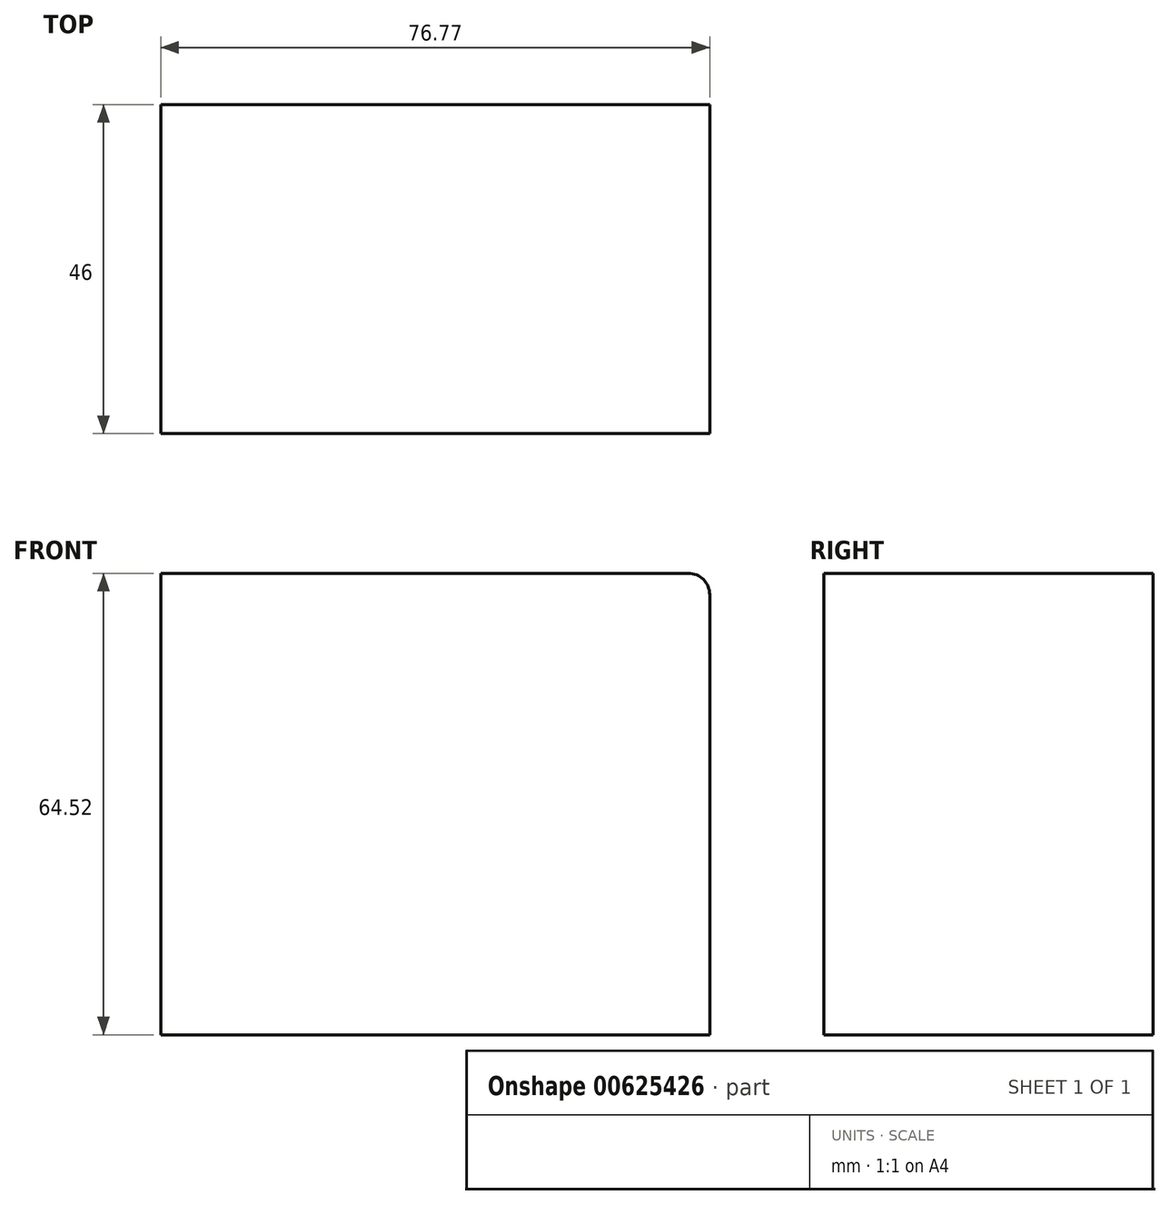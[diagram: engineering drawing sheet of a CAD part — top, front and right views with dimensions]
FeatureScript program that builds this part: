
annotation { "Feature Type Name" : "Feature", "Feature Type Description" : "" }
export const myFeature = defineFeature(function(context is Context, id is Id, definition is map)
    precondition{}
    {
        {
            var Q0;
            Q0=qCreatedBy(makeId("Front.planeOp"),FACE);
            var sketch = newSketch(context, id + "F0", { "sketchPlane" : qUnion([Q0])});
            skLineSegment(sketch, "E0.bottom", {"start": v(-29.7, 32.5) * mm, "end": v(47.07, 32.5) * mm});
            skLineSegment(sketch, "E0.top", {"start": v(-29.7, -32.01) * mm, "end": v(47.07, -32.01) * mm});
            skLineSegment(sketch, "E0.left", {"start": v(-29.7, 32.5) * mm, "end": v(-29.7, -32.01) * mm});
            skLineSegment(sketch, "E0.right", {"start": v(47.07, 32.5) * mm, "end": v(47.07, -32.01) * mm});
            skSolve(sketch);
        }
        {
            var Q0;
            Q0=makeQuery(id+"F0.imprint","IMPRINT",FACE,{"disambiguationData":[TD([[makeQuery(id+"F0.imprint","IMPRINT",EDGE,{"derivedFrom":sQuery(id+"F0.wireOp",EDGE,"E0.bottom")}),-1.0]])]});
            var Q1;
            Q1 = qSketchRegion(id + "F0", true);
            extrude(context, id + "F1", {"entities" : qUnion([Q0, Q1]), "depth" : 46 * mm, "offsetDistance" : 25 * mm});
        }
        {
            var Q0;
            Q0=makeQuery(id+"F1.opExtrude","SWEPT_EDGE",EDGE,{"disambiguationData":[OSD([sQuery(id+"F0.wireOp",EDGE,"E0.bottom"),sQuery(id+"F0.wireOp",EDGE,"E0.right")])]});
            fillet(context, id + "F2", {"entities" : qUnion([Q0]), "radius" : 3 * mm, "tangentPropagation" : true, "allowEdgeOverflow" : false});
        }
    });
